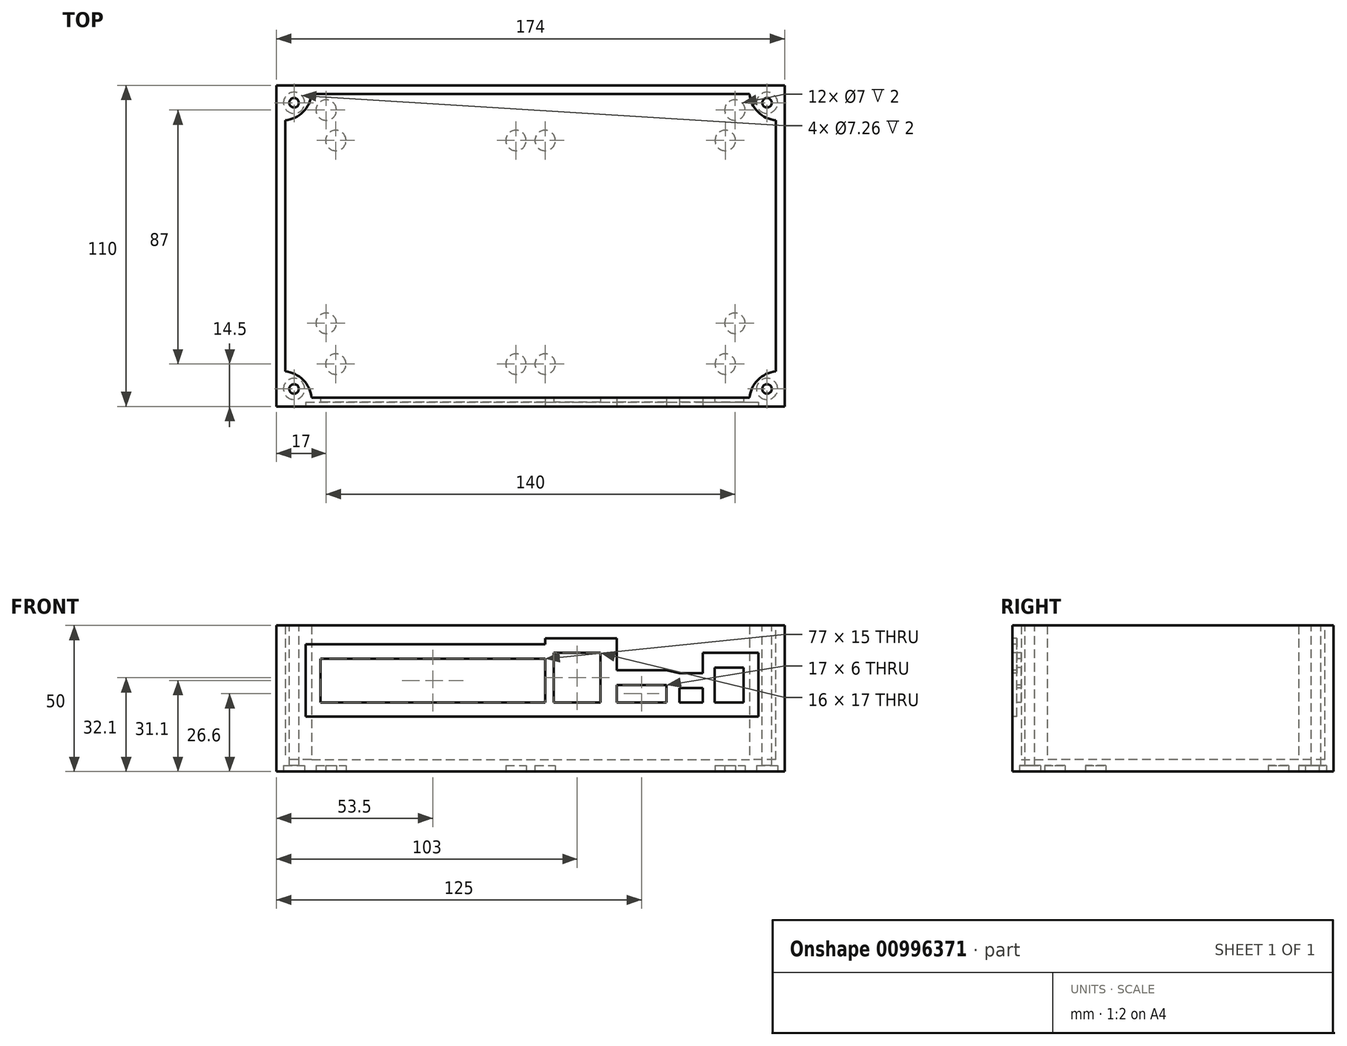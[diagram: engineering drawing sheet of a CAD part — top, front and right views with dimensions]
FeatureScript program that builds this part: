
annotation { "Feature Type Name" : "Feature", "Feature Type Description" : "" }
export const myFeature = defineFeature(function(context is Context, id is Id, definition is map)
    precondition{}
    {
        {
            var Q0;
            Q0=qCreatedBy(makeId("Top.planeOp"),FACE);
            var sketch = newSketch(context, id + "F0", { "sketchPlane" : qUnion([Q0])});
            skLineSegment(sketch, "E0.bottom", {"start": v(-87, -55) * mm, "end": v(87, -55) * mm});
            skLineSegment(sketch, "E0.top", {"start": v(-87, 55) * mm, "end": v(87, 55) * mm});
            skLineSegment(sketch, "E0.left", {"start": v(-87, -55) * mm, "end": v(-87, 55) * mm});
            skLineSegment(sketch, "E0.right", {"start": v(87, -55) * mm, "end": v(87, 55) * mm});
            skPoint(sketch, "E0.middle", {"position": v(0, 0) * mm});
            skSolve(sketch);
        }
        {
            var Q0;
            Q0=makeQuery(id+"F0.imprint","IMPRINT",FACE,{"disambiguationData":[TD([[makeQuery(id+"F0.imprint","IMPRINT",EDGE,{"derivedFrom":sQuery(id+"F0.wireOp",EDGE,"E0.bottom")}),1.0]])]});
            extrude(context, id + "F1", {"entities" : qUnion([Q0]), "depth" : -4 * mm, "offsetDistance" : 25 * mm});
        }
        {
            var Q0;
            Q0=makeQuery(id+"F1.opExtrude","CAP_FACE",FACE,{"disambiguationData":[OSD([sQuery(id+"F0.wireOp",EDGE,"E0.bottom"),sQuery(id+"F0.wireOp",EDGE,"E0.top"),sQuery(id+"F0.wireOp",EDGE,"E0.left"),sQuery(id+"F0.wireOp",EDGE,"E0.right")])],"isStart":true});
            var sketch = newSketch(context, id + "F2", { "sketchPlane" : qUnion([Q0])});
            skLineSegment(sketch, "E1.bottom", {"start": v(-84, 52) * mm, "end": v(84, 52) * mm});
            skLineSegment(sketch, "E1.top", {"start": v(-84, -52) * mm, "end": v(84, -52) * mm});
            skLineSegment(sketch, "E1.left", {"start": v(-84, 52) * mm, "end": v(-84, -52) * mm});
            skLineSegment(sketch, "E1.right", {"start": v(84, 52) * mm, "end": v(84, -52) * mm});
            skPoint(sketch, "E1.middle", {"position": v(0, 0) * mm});
            skLineSegment(sketch, "E2.0", {"start": v(-87, 55) * mm, "end": v(87, 55) * mm});
            skLineSegment(sketch, "E2.1", {"start": v(-87, 55) * mm, "end": v(-87, -55) * mm});
            skLineSegment(sketch, "E2.2", {"start": v(-87, -55) * mm, "end": v(87, -55) * mm});
            skLineSegment(sketch, "E2.3", {"start": v(87, 55) * mm, "end": v(87, -55) * mm});
            skSolve(sketch);
        }
        {
            var Q0;
            Q0=makeQuery(id+"F2.imprint","IMPRINT",FACE,{"disambiguationData":[TD([[makeQuery(id+"F2.imprint","IMPRINT",EDGE,{"derivedFrom":sQuery(id+"F2.wireOp",EDGE,"E1.bottom")}),1.0]])]});
            extrude(context, id + "F3", {"entities" : qUnion([Q0]), "operationType" : NewBodyOperationType.ADD, "depth" : 46 * mm, "offsetDistance" : 25 * mm});
        }
        {
            var Q0;
            Q0=makeQuery(id+"F1.opExtrude","CAP_FACE",FACE,{"disambiguationData":[OSD([sQuery(id+"F0.wireOp",EDGE,"E0.bottom"),sQuery(id+"F0.wireOp",EDGE,"E0.top"),sQuery(id+"F0.wireOp",EDGE,"E0.left"),sQuery(id+"F0.wireOp",EDGE,"E0.right")])],"isStart":false});
            var sketch = newSketch(context, id + "F4", { "sketchPlane" : qUnion([Q0])});
            skLineSegment(sketch, "E3.bottom", {"start": v(-74, 50.5) * mm, "end": v(74, 50.5) * mm});
            skLineSegment(sketch, "E3.top", {"start": v(-74, -50.5) * mm, "end": v(74, -50.5) * mm});
            skLineSegment(sketch, "E3.left", {"start": v(-74, 50.5) * mm, "end": v(-74, -50.5) * mm});
            skLineSegment(sketch, "E3.right", {"start": v(74, 50.5) * mm, "end": v(74, -50.5) * mm});
            skPoint(sketch, "E3.middle", {"position": v(0, 0) * mm});
            skLineSegment(sketch, "E4.bottom", {"start": v(-65.7, 44.5) * mm, "end": v(-4, 44.5) * mm, "construction": true});
            skLineSegment(sketch, "E4.top", {"start": v(-65.7, -32.1) * mm, "end": v(-4, -32.1) * mm, "construction": true});
            skLineSegment(sketch, "E4.left", {"start": v(-65.7, 44.5) * mm, "end": v(-65.7, -32.1) * mm, "construction": true});
            skLineSegment(sketch, "E4.right", {"start": v(-4, 44.5) * mm, "end": v(-4, -32.1) * mm, "construction": true});
            skLineSegment(sketch, "E5.bottom", {"start": v(4, 44.5) * mm, "end": v(65.7, 44.5) * mm, "construction": true});
            skLineSegment(sketch, "E5.top", {"start": v(4, -32.1) * mm, "end": v(65.7, -32.1) * mm, "construction": true});
            skLineSegment(sketch, "E5.left", {"start": v(4, 44.5) * mm, "end": v(4, -32.1) * mm, "construction": true});
            skLineSegment(sketch, "E5.right", {"start": v(65.7, 44.5) * mm, "end": v(65.7, -32.1) * mm, "construction": true});
            skCircle(sketch, "E6", {"center": v(-65.7, 44.5) * mm, "radius": 1.63 * mm});
            skCircle(sketch, "E7", {"center": v(-4, 44.5) * mm, "radius": 1.63 * mm});
            skCircle(sketch, "E8", {"center": v(-65.7, -32.1) * mm, "radius": 1.63 * mm});
            skCircle(sketch, "E9", {"center": v(-4, -32.1) * mm, "radius": 1.63 * mm});
            skCircle(sketch, "E10", {"center": v(4, -32.1) * mm, "radius": 1.63 * mm});
            skCircle(sketch, "E11", {"center": v(65.7, -32.1) * mm, "radius": 1.63 * mm});
            skCircle(sketch, "E12", {"center": v(65.7, 44.5) * mm, "radius": 1.63 * mm});
            skCircle(sketch, "E13", {"center": v(4, 44.5) * mm, "radius": 1.5 * mm});
            skCircle(sketch, "E14.0", {"center": v(-65.7, 44.5) * mm, "radius": 3.63 * mm});
            skCircle(sketch, "E15.0", {"center": v(-4, 44.5) * mm, "radius": 3.63 * mm});
            skCircle(sketch, "E16.0", {"center": v(4, 44.5) * mm, "radius": 3.5 * mm});
            skCircle(sketch, "E17.0", {"center": v(65.7, 44.5) * mm, "radius": 3.63 * mm});
            skCircle(sketch, "E18.0", {"center": v(65.7, -32.1) * mm, "radius": 3.63 * mm});
            skCircle(sketch, "E19.0", {"center": v(4, -32.1) * mm, "radius": 3.63 * mm});
            skCircle(sketch, "E20.0", {"center": v(-4, -32.1) * mm, "radius": 3.63 * mm});
            skCircle(sketch, "E21.0", {"center": v(-65.7, -32.1) * mm, "radius": 3.63 * mm});
            skCircle(sketch, "E22", {"center": v(-70, -46.5) * mm, "radius": 1.63 * mm});
            skCircle(sketch, "E23.0", {"center": v(-70, -46.5) * mm, "radius": 3.63 * mm});
            skCircle(sketch, "E24", {"center": v(-70, 26.5) * mm, "radius": 1.63 * mm});
            skCircle(sketch, "E25.0", {"center": v(-70, 26.5) * mm, "radius": 3.63 * mm});
            skCircle(sketch, "E26", {"center": v(70, -46.5) * mm, "radius": 1.63 * mm});
            skCircle(sketch, "E27.0", {"center": v(70, -46.5) * mm, "radius": 3.63 * mm});
            skCircle(sketch, "E28", {"center": v(70, 26.5) * mm, "radius": 1.63 * mm});
            skCircle(sketch, "E29.0", {"center": v(70, 26.5) * mm, "radius": 3.63 * mm});
            skSolve(sketch);
        }
        {
            var Q0;
            Q0=makeQuery(id+"F1.opExtrude","CAP_FACE",FACE,{"disambiguationData":[OSD([sQuery(id+"F0.wireOp",EDGE,"E0.bottom"),sQuery(id+"F0.wireOp",EDGE,"E0.top"),sQuery(id+"F0.wireOp",EDGE,"E0.left"),sQuery(id+"F0.wireOp",EDGE,"E0.right")])],"isStart":false});
            var sketch = newSketch(context, id + "F5", { "sketchPlane" : qUnion([Q0])});
            skCircle(sketch, "E30.0", {"center": v(-66.7, 40.5) * mm, "radius": 3.5 * mm});
            skCircle(sketch, "E31.0", {"center": v(-70, 26.5) * mm, "radius": 3.5 * mm});
            skCircle(sketch, "E32.0", {"center": v(-5, 40.5) * mm, "radius": 3.5 * mm});
            skCircle(sketch, "E33.0", {"center": v(5, 40.5) * mm, "radius": 3.5 * mm});
            skCircle(sketch, "E34.0", {"center": v(66.7, 40.5) * mm, "radius": 3.5 * mm});
            skCircle(sketch, "E35.0", {"center": v(70, 26.5) * mm, "radius": 3.5 * mm});
            skCircle(sketch, "E36.0", {"center": v(66.7, -36.1) * mm, "radius": 3.5 * mm});
            skCircle(sketch, "E37.0", {"center": v(70, -46.5) * mm, "radius": 3.5 * mm});
            skCircle(sketch, "E38.0", {"center": v(5, -36.1) * mm, "radius": 3.5 * mm});
            skCircle(sketch, "E39.0", {"center": v(-5, -36.1) * mm, "radius": 3.5 * mm});
            skCircle(sketch, "E40.0", {"center": v(-66.7, -36.1) * mm, "radius": 3.5 * mm});
            skCircle(sketch, "E41.0", {"center": v(-70, -46.5) * mm, "radius": 3.5 * mm});
            skLineSegment(sketch, "E42.0", {"start": v(-92, -60) * mm, "end": v(92, -60) * mm});
            skLineSegment(sketch, "E42.1", {"start": v(-92, 60) * mm, "end": v(-92, -60) * mm});
            skLineSegment(sketch, "E42.2", {"start": v(92, 60) * mm, "end": v(-92, 60) * mm});
            skLineSegment(sketch, "E42.3", {"start": v(92, -60) * mm, "end": v(92, 60) * mm});
            skSolve(sketch);
        }
        {
            var Q0;
            Q0=makeQuery(id+"F5.imprint","IMPRINT",FACE,{"disambiguationData":[TD([[makeQuery(id+"F5.imprint","IMPRINT",EDGE,{"derivedFrom":sQuery(id+"F5.wireOp",EDGE,"E30.0")}),1.0]])]});
            var Q1;
            Q1=makeQuery(id+"F5.imprint","IMPRINT",FACE,{"disambiguationData":[TD([[makeQuery(id+"F5.imprint","IMPRINT",EDGE,{"derivedFrom":sQuery(id+"F5.wireOp",EDGE,"E31.0")}),1.0]])]});
            var Q2;
            Q2=makeQuery(id+"F5.imprint","IMPRINT",FACE,{"disambiguationData":[TD([[makeQuery(id+"F5.imprint","IMPRINT",EDGE,{"derivedFrom":sQuery(id+"F5.wireOp",EDGE,"E40.0")}),1.0]])]});
            var Q3;
            Q3=makeQuery(id+"F5.imprint","IMPRINT",FACE,{"disambiguationData":[TD([[makeQuery(id+"F5.imprint","IMPRINT",EDGE,{"derivedFrom":sQuery(id+"F5.wireOp",EDGE,"E41.0")}),1.0]])]});
            var Q4;
            Q4=makeQuery(id+"F5.imprint","IMPRINT",FACE,{"disambiguationData":[TD([[makeQuery(id+"F5.imprint","IMPRINT",EDGE,{"derivedFrom":sQuery(id+"F5.wireOp",EDGE,"E39.0")}),1.0]])]});
            var Q5;
            Q5=makeQuery(id+"F5.imprint","IMPRINT",FACE,{"disambiguationData":[TD([[makeQuery(id+"F5.imprint","IMPRINT",EDGE,{"derivedFrom":sQuery(id+"F5.wireOp",EDGE,"E38.0")}),1.0]])]});
            var Q6;
            Q6=makeQuery(id+"F5.imprint","IMPRINT",FACE,{"disambiguationData":[TD([[makeQuery(id+"F5.imprint","IMPRINT",EDGE,{"derivedFrom":sQuery(id+"F5.wireOp",EDGE,"E32.0")}),1.0]])]});
            var Q7;
            Q7=makeQuery(id+"F5.imprint","IMPRINT",FACE,{"disambiguationData":[TD([[makeQuery(id+"F5.imprint","IMPRINT",EDGE,{"derivedFrom":sQuery(id+"F5.wireOp",EDGE,"E33.0")}),1.0]])]});
            var Q8;
            Q8=makeQuery(id+"F5.imprint","IMPRINT",FACE,{"disambiguationData":[TD([[makeQuery(id+"F5.imprint","IMPRINT",EDGE,{"derivedFrom":sQuery(id+"F5.wireOp",EDGE,"E34.0")}),1.0]])]});
            var Q9;
            Q9=makeQuery(id+"F5.imprint","IMPRINT",FACE,{"disambiguationData":[TD([[makeQuery(id+"F5.imprint","IMPRINT",EDGE,{"derivedFrom":sQuery(id+"F5.wireOp",EDGE,"E35.0")}),1.0]])]});
            var Q10;
            Q10=makeQuery(id+"F5.imprint","IMPRINT",FACE,{"disambiguationData":[TD([[makeQuery(id+"F5.imprint","IMPRINT",EDGE,{"derivedFrom":sQuery(id+"F5.wireOp",EDGE,"E36.0")}),1.0]])]});
            var Q11;
            Q11=makeQuery(id+"F5.imprint","IMPRINT",FACE,{"disambiguationData":[TD([[makeQuery(id+"F5.imprint","IMPRINT",EDGE,{"derivedFrom":sQuery(id+"F5.wireOp",EDGE,"E37.0")}),1.0]])]});
            extrude(context, id + "F6", {"entities" : qUnion([Q0, Q1, Q2, Q3, Q4, Q5, Q6, Q7, Q8, Q9, Q10, Q11]), "operationType" : NewBodyOperationType.REMOVE, "depth" : -2 * mm, "offsetDistance" : 25 * mm});
        }
        {
            var Q0;
            Q0=makeQuery(id+"F3.boolean.opBoolean","MERGE",FACE,{"derivedFrom":[makeQuery(id+"F1.opExtrude","SWEPT_FACE",FACE,{"disambiguationData":[OSD([sQuery(id+"F0.wireOp",EDGE,"E0.bottom")])]}),makeQuery(id+"F3.opExtrude","SWEPT_FACE",FACE,{"disambiguationData":[OSD([sQuery(id+"F2.wireOp",EDGE,"E2.2")])]})]});
            var sketch = newSketch(context, id + "F7", { "sketchPlane" : qUnion([Q0])});
            skLineSegment(sketch, "E43", {"start": v(-100.46, 19.6) * mm, "end": v(103.84, 19.6) * mm, "construction": true});
            skLineSegment(sketch, "E44", {"start": v(0, -31) * mm, "end": v(0, 52.42) * mm, "construction": true});
            skLineSegment(sketch, "E45.bottom", {"start": v(-74, 59.6) * mm, "end": v(74, 59.6) * mm, "construction": true});
            skLineSegment(sketch, "E45.top", {"start": v(-74, -20.4) * mm, "end": v(74, -20.4) * mm, "construction": true});
            skLineSegment(sketch, "E45.left", {"start": v(-74, 59.6) * mm, "end": v(-74, -20.4) * mm, "construction": true});
            skLineSegment(sketch, "E45.right", {"start": v(74, 59.6) * mm, "end": v(74, -20.4) * mm, "construction": true});
            skPoint(sketch, "E45.middle", {"position": v(0, 19.6) * mm});
            skLineSegment(sketch, "E46", {"start": v(-33.5, 53.59) * mm, "end": v(-33.5, -6.96) * mm, "construction": true});
            skLineSegment(sketch, "E47", {"start": v(16, 52.07) * mm, "end": v(16, -12.35) * mm, "construction": true});
            skLineSegment(sketch, "E48", {"start": v(38, 50.3) * mm, "end": v(38, -12.83) * mm, "construction": true});
            skLineSegment(sketch, "E49", {"start": v(55, 49.17) * mm, "end": v(55, -12.18) * mm, "construction": true});
            skLineSegment(sketch, "E50", {"start": v(68, 54.65) * mm, "end": v(68, -10.1) * mm, "construction": true});
            skPoint(sketch, "E51.middle", {"position": v(16, 19.6) * mm});
            skPoint(sketch, "E52.middle", {"position": v(38, 19.6) * mm});
            skPoint(sketch, "E53.middle", {"position": v(55, 19.6) * mm});
            skPoint(sketch, "E54.middle", {"position": v(68, 19.6) * mm});
            skPoint(sketch, "E55.middle", {"position": v(-33.5, 19.6) * mm});
            skLineSegment(sketch, "E56.bottom", {"start": v(-33.5, 19.6) * mm, "end": v(-72, 19.6) * mm});
            skLineSegment(sketch, "E56.top", {"start": v(-33.5, 34.6) * mm, "end": v(-72, 34.6) * mm});
            skLineSegment(sketch, "E56.left", {"start": v(-33.5, 19.6) * mm, "end": v(-33.5, 34.6) * mm});
            skLineSegment(sketch, "E56.right", {"start": v(-72, 19.6) * mm, "end": v(-72, 34.6) * mm});
            skLineSegment(sketch, "E57.bottom", {"start": v(-33.5, 19.6) * mm, "end": v(5, 19.6) * mm});
            skLineSegment(sketch, "E57.top", {"start": v(-33.5, 34.6) * mm, "end": v(5, 34.6) * mm});
            skLineSegment(sketch, "E57.right", {"start": v(5, 19.6) * mm, "end": v(5, 34.6) * mm});
            skLineSegment(sketch, "E58.bottom", {"start": v(16, 19.6) * mm, "end": v(8, 19.6) * mm});
            skLineSegment(sketch, "E58.top", {"start": v(16, 36.6) * mm, "end": v(8, 36.6) * mm});
            skLineSegment(sketch, "E58.left", {"start": v(16, 19.6) * mm, "end": v(16, 36.6) * mm});
            skLineSegment(sketch, "E58.right", {"start": v(8, 19.6) * mm, "end": v(8, 36.6) * mm});
            skLineSegment(sketch, "E59.bottom", {"start": v(16, 19.6) * mm, "end": v(24, 19.6) * mm});
            skLineSegment(sketch, "E59.top", {"start": v(16, 36.6) * mm, "end": v(24, 36.6) * mm});
            skLineSegment(sketch, "E59.right", {"start": v(24, 19.6) * mm, "end": v(24, 36.6) * mm});
            skLineSegment(sketch, "E60.bottom", {"start": v(38, 19.6) * mm, "end": v(29.5, 19.6) * mm});
            skLineSegment(sketch, "E60.top", {"start": v(38, 25.6) * mm, "end": v(29.5, 25.6) * mm});
            skLineSegment(sketch, "E60.left", {"start": v(38, 19.6) * mm, "end": v(38, 25.6) * mm});
            skLineSegment(sketch, "E60.right", {"start": v(29.5, 19.6) * mm, "end": v(29.5, 25.6) * mm});
            skLineSegment(sketch, "E61.bottom", {"start": v(38, 19.6) * mm, "end": v(46.5, 19.6) * mm});
            skLineSegment(sketch, "E61.top", {"start": v(38, 25.6) * mm, "end": v(46.5, 25.6) * mm});
            skLineSegment(sketch, "E61.right", {"start": v(46.5, 19.6) * mm, "end": v(46.5, 25.6) * mm});
            skLineSegment(sketch, "E62.bottom", {"start": v(55, 19.6) * mm, "end": v(51, 19.6) * mm});
            skLineSegment(sketch, "E62.top", {"start": v(55, 24.6) * mm, "end": v(51, 24.6) * mm});
            skLineSegment(sketch, "E62.left", {"start": v(55, 19.6) * mm, "end": v(55, 24.6) * mm});
            skLineSegment(sketch, "E62.right", {"start": v(51, 19.6) * mm, "end": v(51, 24.6) * mm});
            skLineSegment(sketch, "E63.bottom", {"start": v(55, 19.6) * mm, "end": v(59, 19.6) * mm});
            skLineSegment(sketch, "E63.top", {"start": v(55, 24.6) * mm, "end": v(59, 24.6) * mm});
            skLineSegment(sketch, "E63.right", {"start": v(59, 19.6) * mm, "end": v(59, 24.6) * mm});
            skLineSegment(sketch, "E64.bottom", {"start": v(68, 19.6) * mm, "end": v(63, 19.6) * mm});
            skLineSegment(sketch, "E64.top", {"start": v(68, 31.6) * mm, "end": v(63, 31.6) * mm});
            skLineSegment(sketch, "E64.left", {"start": v(68, 19.6) * mm, "end": v(68, 31.6) * mm});
            skLineSegment(sketch, "E64.right", {"start": v(63, 19.6) * mm, "end": v(63, 31.6) * mm});
            skLineSegment(sketch, "E65.bottom", {"start": v(68, 19.6) * mm, "end": v(73, 19.6) * mm});
            skLineSegment(sketch, "E65.top", {"start": v(68, 31.6) * mm, "end": v(73, 31.6) * mm});
            skLineSegment(sketch, "E65.right", {"start": v(73, 19.6) * mm, "end": v(73, 31.6) * mm});
            skLineSegment(sketch, "E66.0", {"start": v(-77, 19.8) * mm, "end": v(-77, 34.6) * mm});
            skLineSegment(sketch, "E67.0", {"start": v(-33.5, 39.6) * mm, "end": v(-72, 39.6) * mm});
            skLineSegment(sketch, "E68.0", {"start": v(-33.5, 39.6) * mm, "end": v(5, 39.6) * mm});
            skLineSegment(sketch, "E69.0", {"start": v(16, 41.6) * mm, "end": v(8, 41.6) * mm});
            skLineSegment(sketch, "E70.0", {"start": v(16, 41.6) * mm, "end": v(24, 41.6) * mm});
            skLineSegment(sketch, "E71.0", {"start": v(38, 30.6) * mm, "end": v(29.5, 30.6) * mm});
            skLineSegment(sketch, "E72.0", {"start": v(38, 30.6) * mm, "end": v(46.5, 30.6) * mm});
            skLineSegment(sketch, "E73.0", {"start": v(55, 29.6) * mm, "end": v(51, 29.6) * mm});
            skLineSegment(sketch, "E74.0", {"start": v(55, 29.6) * mm, "end": v(59, 29.6) * mm});
            skLineSegment(sketch, "E75.0", {"start": v(68, 36.6) * mm, "end": v(63, 36.6) * mm});
            skLineSegment(sketch, "E76.0", {"start": v(68, 36.6) * mm, "end": v(73, 36.6) * mm});
            skLineSegment(sketch, "E77.0", {"start": v(78, 19.6) * mm, "end": v(78, 31.6) * mm});
            skLineSegment(sketch, "E78", {"start": v(-77, 34.6) * mm, "end": v(-77, 39.6) * mm});
            skLineSegment(sketch, "E79", {"start": v(-77, 39.6) * mm, "end": v(-72, 39.6) * mm});
            skLineSegment(sketch, "E80", {"start": v(5, 39.6) * mm, "end": v(5, 41.6) * mm});
            skLineSegment(sketch, "E81", {"start": v(5, 41.6) * mm, "end": v(8, 41.6) * mm});
            skLineSegment(sketch, "E82", {"start": v(24, 41.6) * mm, "end": v(29.5, 41.6) * mm});
            skLineSegment(sketch, "E83", {"start": v(29.5, 41.6) * mm, "end": v(29.5, 30.6) * mm});
            skLineSegment(sketch, "E84", {"start": v(46.5, 30.6) * mm, "end": v(51, 29.6) * mm});
            skLineSegment(sketch, "E85", {"start": v(59, 29.6) * mm, "end": v(59, 36.6) * mm});
            skLineSegment(sketch, "E86", {"start": v(59, 36.6) * mm, "end": v(63, 36.6) * mm});
            skLineSegment(sketch, "E87", {"start": v(73, 36.6) * mm, "end": v(78, 36.6) * mm});
            skLineSegment(sketch, "E88", {"start": v(78, 36.6) * mm, "end": v(78, 31.6) * mm});
            skLineSegment(sketch, "E89", {"start": v(-77, 19.8) * mm, "end": v(-77, 14.8) * mm});
            skLineSegment(sketch, "E90", {"start": v(-77, 14.8) * mm, "end": v(78, 14.8) * mm});
            skLineSegment(sketch, "E91", {"start": v(78, 14.8) * mm, "end": v(78, 19.6) * mm});
            skSolve(sketch);
        }
        {
            var Q0;
            Q0=makeQuery(id+"F7.imprint","IMPRINT",FACE,{"disambiguationData":[TD([[makeQuery(id+"F7.imprint","IMPRINT",EDGE,{"derivedFrom":sQuery(id+"F7.wireOp",EDGE,"E56.bottom")}),-1.0]])]});
            var Q1;
            Q1=makeQuery(id+"F7.imprint","IMPRINT",FACE,{"disambiguationData":[TD([[makeQuery(id+"F7.imprint","IMPRINT",EDGE,{"derivedFrom":sQuery(id+"F7.wireOp",EDGE,"E57.bottom")}),1.0]])]});
            var Q2;
            Q2=makeQuery(id+"F7.imprint","IMPRINT",FACE,{"disambiguationData":[TD([[makeQuery(id+"F7.imprint","IMPRINT",EDGE,{"derivedFrom":sQuery(id+"F7.wireOp",EDGE,"E58.bottom")}),-1.0]])]});
            var Q3;
            Q3=makeQuery(id+"F7.imprint","IMPRINT",FACE,{"disambiguationData":[TD([[makeQuery(id+"F7.imprint","IMPRINT",EDGE,{"derivedFrom":sQuery(id+"F7.wireOp",EDGE,"E59.bottom")}),1.0]])]});
            var Q4;
            Q4=makeQuery(id+"F7.imprint","IMPRINT",FACE,{"disambiguationData":[TD([[makeQuery(id+"F7.imprint","IMPRINT",EDGE,{"derivedFrom":sQuery(id+"F7.wireOp",EDGE,"E60.bottom")}),-1.0]])]});
            var Q5;
            Q5=makeQuery(id+"F7.imprint","IMPRINT",FACE,{"disambiguationData":[TD([[makeQuery(id+"F7.imprint","IMPRINT",EDGE,{"derivedFrom":sQuery(id+"F7.wireOp",EDGE,"E61.bottom")}),1.0]])]});
            var Q6;
            Q6=makeQuery(id+"F7.imprint","IMPRINT",FACE,{"disambiguationData":[TD([[makeQuery(id+"F7.imprint","IMPRINT",EDGE,{"derivedFrom":sQuery(id+"F7.wireOp",EDGE,"E62.bottom")}),-1.0]])]});
            var Q7;
            Q7=makeQuery(id+"F7.imprint","IMPRINT",FACE,{"disambiguationData":[TD([[makeQuery(id+"F7.imprint","IMPRINT",EDGE,{"derivedFrom":sQuery(id+"F7.wireOp",EDGE,"E63.bottom")}),1.0]])]});
            var Q8;
            Q8=makeQuery(id+"F7.imprint","IMPRINT",FACE,{"disambiguationData":[TD([[makeQuery(id+"F7.imprint","IMPRINT",EDGE,{"derivedFrom":sQuery(id+"F7.wireOp",EDGE,"E64.bottom")}),-1.0]])]});
            var Q9;
            Q9=makeQuery(id+"F7.imprint","IMPRINT",FACE,{"disambiguationData":[TD([[makeQuery(id+"F7.imprint","IMPRINT",EDGE,{"derivedFrom":sQuery(id+"F7.wireOp",EDGE,"E65.bottom")}),1.0]])]});
            extrude(context, id + "F8", {"entities" : qUnion([Q0, Q1, Q2, Q3, Q4, Q5, Q6, Q7, Q8, Q9]), "operationType" : NewBodyOperationType.REMOVE, "oppositeDirection" : true, "depth" : 3 * mm, "offsetDistance" : 25 * mm});
        }
        {
            var Q0;
            Q0=makeQuery(id+"F3.opExtrude","CAP_FACE",FACE,{"disambiguationData":[OSD([sQuery(id+"F2.wireOp",EDGE,"E1.bottom"),sQuery(id+"F2.wireOp",EDGE,"E1.top"),sQuery(id+"F2.wireOp",EDGE,"E1.left"),sQuery(id+"F2.wireOp",EDGE,"E1.right"),sQuery(id+"F2.wireOp",EDGE,"E2.0"),sQuery(id+"F2.wireOp",EDGE,"E2.1"),sQuery(id+"F2.wireOp",EDGE,"E2.2"),sQuery(id+"F2.wireOp",EDGE,"E2.3")])],"isStart":false});
            var sketch = newSketch(context, id + "F9", { "sketchPlane" : qUnion([Q0])});
            skLineSegment(sketch, "E92.bottom", {"start": v(-87, 55) * mm, "end": v(-75, 55) * mm});
            skLineSegment(sketch, "E92.top", {"start": v(-87, 43) * mm, "end": v(-75, 43) * mm});
            skLineSegment(sketch, "E92.left", {"start": v(-87, 55) * mm, "end": v(-87, 43) * mm});
            skLineSegment(sketch, "E92.right", {"start": v(-75, 55) * mm, "end": v(-75, 43) * mm});
            skLineSegment(sketch, "E93.bottom", {"start": v(87, 55) * mm, "end": v(75, 55) * mm});
            skLineSegment(sketch, "E93.top", {"start": v(87, 43) * mm, "end": v(75, 43) * mm});
            skLineSegment(sketch, "E93.left", {"start": v(87, 55) * mm, "end": v(87, 43) * mm});
            skLineSegment(sketch, "E93.right", {"start": v(75, 55) * mm, "end": v(75, 43) * mm});
            skLineSegment(sketch, "E94.bottom", {"start": v(87, -55) * mm, "end": v(75, -55) * mm});
            skLineSegment(sketch, "E94.top", {"start": v(87, -43) * mm, "end": v(75, -43) * mm});
            skLineSegment(sketch, "E94.left", {"start": v(87, -55) * mm, "end": v(87, -43) * mm});
            skLineSegment(sketch, "E94.right", {"start": v(75, -55) * mm, "end": v(75, -43) * mm});
            skLineSegment(sketch, "E95.bottom", {"start": v(-87, -55) * mm, "end": v(-75, -55) * mm});
            skLineSegment(sketch, "E95.top", {"start": v(-87, -43) * mm, "end": v(-75, -43) * mm});
            skLineSegment(sketch, "E95.left", {"start": v(-87, -55) * mm, "end": v(-87, -43) * mm});
            skLineSegment(sketch, "E95.right", {"start": v(-75, -55) * mm, "end": v(-75, -43) * mm});
            skCircle(sketch, "E96", {"center": v(-81, 49) * mm, "radius": 1.63 * mm});
            skPoint(sketch, "E96.centerSnap0", {"position": v(-81, 55) * mm});
            skPoint(sketch, "E96.centerSnap1", {"position": v(-87, 49) * mm});
            skCircle(sketch, "E97", {"center": v(81, 49) * mm, "radius": 1.63 * mm});
            skPoint(sketch, "E97.centerSnap0", {"position": v(75, 49) * mm});
            skPoint(sketch, "E97.centerSnap1", {"position": v(81, 43) * mm});
            skCircle(sketch, "E98", {"center": v(-81, -49) * mm, "radius": 1.63 * mm});
            skPoint(sketch, "E98.centerSnap0", {"position": v(-87, -49) * mm});
            skPoint(sketch, "E98.centerSnap1", {"position": v(-81, -43) * mm});
            skCircle(sketch, "E99", {"center": v(81, -49) * mm, "radius": 1.63 * mm});
            skPoint(sketch, "E99.centerSnap0", {"position": v(81, -55) * mm});
            skPoint(sketch, "E99.centerSnap1", {"position": v(87, -49) * mm});
            skSolve(sketch);
        }
        {
            var Q0;
            Q0=makeQuery(id+"F9.imprint","IMPRINT",FACE,{"disambiguationData":[TD([[makeQuery(id+"F9.imprint","IMPRINT",EDGE,{"derivedFrom":sQuery(id+"F9.wireOp",EDGE,"E96")}),-1.0]])]});
            var Q1;
            {var subQ1=sQuery(id+"F9.wireOp",EDGE,"E92.bottom");Q1=makeQuery(id+"F9.imprint","IMPRINT",FACE,{"disambiguationData":[TD([[makeQuery(id+"F9.imprint","IMPRINT",EDGE,{"derivedFrom":subQ1}),-1.0]])]});}
            var Q2;
            {var subQ1=sQuery(id+"F9.wireOp",EDGE,"E93.bottom");Q2=makeQuery(id+"F9.imprint","IMPRINT",FACE,{"disambiguationData":[TD([[makeQuery(id+"F9.imprint","IMPRINT",EDGE,{"derivedFrom":subQ1}),-1.0]])]});}
            var Q3;
            Q3=makeQuery(id+"F9.imprint","IMPRINT",FACE,{"disambiguationData":[TD([[makeQuery(id+"F9.imprint","IMPRINT",EDGE,{"derivedFrom":sQuery(id+"F9.wireOp",EDGE,"E97")}),-1.0]])]});
            var Q4;
            {var subQ1=sQuery(id+"F9.wireOp",EDGE,"E94.bottom");Q4=makeQuery(id+"F9.imprint","IMPRINT",FACE,{"disambiguationData":[TD([[makeQuery(id+"F9.imprint","IMPRINT",EDGE,{"derivedFrom":subQ1}),1.0]])]});}
            var Q5;
            Q5=makeQuery(id+"F9.imprint","IMPRINT",FACE,{"disambiguationData":[TD([[makeQuery(id+"F9.imprint","IMPRINT",EDGE,{"derivedFrom":sQuery(id+"F9.wireOp",EDGE,"E99")}),-1.0]])]});
            var Q6;
            Q6=makeQuery(id+"F9.imprint","IMPRINT",FACE,{"disambiguationData":[TD([[makeQuery(id+"F9.imprint","IMPRINT",EDGE,{"derivedFrom":sQuery(id+"F9.wireOp",EDGE,"E98")}),-1.0]])]});
            var Q7;
            {var subQ1=sQuery(id+"F9.wireOp",EDGE,"E95.bottom");Q7=makeQuery(id+"F9.imprint","IMPRINT",FACE,{"disambiguationData":[TD([[makeQuery(id+"F9.imprint","IMPRINT",EDGE,{"derivedFrom":subQ1}),1.0]])]});}
            extrude(context, id + "F10", {"entities" : qUnion([Q0, Q1, Q2, Q3, Q4, Q5, Q6, Q7]), "operationType" : NewBodyOperationType.ADD, "oppositeDirection" : true, "depth" : 46 * mm, "offsetDistance" : 25 * mm});
        }
        {
            var Q0;
            Q0=makeQuery(id+"F9.imprint","IMPRINT",FACE,{"disambiguationData":[TD([[makeQuery(id+"F9.imprint","IMPRINT",EDGE,{"derivedFrom":sQuery(id+"F9.wireOp",EDGE,"E96")}),1.0]])]});
            var Q1;
            Q1=makeQuery(id+"F9.imprint","IMPRINT",FACE,{"disambiguationData":[TD([[makeQuery(id+"F9.imprint","IMPRINT",EDGE,{"derivedFrom":sQuery(id+"F9.wireOp",EDGE,"E97")}),1.0]])]});
            var Q2;
            Q2=makeQuery(id+"F9.imprint","IMPRINT",FACE,{"disambiguationData":[TD([[makeQuery(id+"F9.imprint","IMPRINT",EDGE,{"derivedFrom":sQuery(id+"F9.wireOp",EDGE,"E99")}),1.0]])]});
            var Q3;
            Q3=makeQuery(id+"F9.imprint","IMPRINT",FACE,{"disambiguationData":[TD([[makeQuery(id+"F9.imprint","IMPRINT",EDGE,{"derivedFrom":sQuery(id+"F9.wireOp",EDGE,"E98")}),1.0]])]});
            extrude(context, id + "F11", {"entities" : qUnion([Q0, Q1, Q2, Q3]), "operationType" : NewBodyOperationType.REMOVE, "endBound" : BoundingType.THROUGH_ALL, "oppositeDirection" : true, "depth" : 25 * mm, "offsetDistance" : 25 * mm});
        }
        {
            var Q0;
            Q0=makeQuery(id+"F10.opExtrude","SWEPT_EDGE",EDGE,{"disambiguationData":[OSD([sQuery(id+"F9.wireOp",EDGE,"E92.top"),sQuery(id+"F9.wireOp",EDGE,"E92.right")])]});
            var Q1;
            Q1=makeQuery(id+"F10.opExtrude","SWEPT_EDGE",EDGE,{"disambiguationData":[OSD([sQuery(id+"F9.wireOp",EDGE,"E93.top"),sQuery(id+"F9.wireOp",EDGE,"E93.right")])]});
            var Q2;
            Q2=makeQuery(id+"F10.opExtrude","SWEPT_EDGE",EDGE,{"disambiguationData":[OSD([sQuery(id+"F9.wireOp",EDGE,"E95.top"),sQuery(id+"F9.wireOp",EDGE,"E95.right")])]});
            var Q3;
            Q3=makeQuery(id+"F10.opExtrude","SWEPT_EDGE",EDGE,{"disambiguationData":[OSD([sQuery(id+"F9.wireOp",EDGE,"E94.top"),sQuery(id+"F9.wireOp",EDGE,"E94.right")])]});
            fillet(context, id + "F12", {"entities" : qUnion([Q0, Q1, Q2, Q3]), "radius" : 10 * mm, "tangentPropagation" : true, "allowEdgeOverflow" : false});
        }
        {
            var Q0;
            Q0=makeQuery(id+"F1.opExtrude","CAP_FACE",FACE,{"disambiguationData":[OSD([sQuery(id+"F0.wireOp",EDGE,"E0.bottom"),sQuery(id+"F0.wireOp",EDGE,"E0.top"),sQuery(id+"F0.wireOp",EDGE,"E0.left"),sQuery(id+"F0.wireOp",EDGE,"E0.right")])],"isStart":false});
            var sketch = newSketch(context, id + "F13", { "sketchPlane" : qUnion([Q0])});
            skCircle(sketch, "E100.0", {"center": v(-81, 49) * mm, "radius": 3.63 * mm});
            skCircle(sketch, "E101.0", {"center": v(81, 49) * mm, "radius": 3.63 * mm});
            skCircle(sketch, "E102.0", {"center": v(81, -49) * mm, "radius": 3.63 * mm});
            skCircle(sketch, "E103.0", {"center": v(-81, -49) * mm, "radius": 3.63 * mm});
            skSolve(sketch);
        }
        {
            var Q0;
            Q0=makeQuery(id+"F13.imprint","IMPRINT",FACE,{"disambiguationData":[TD([[makeQuery(id+"F13.imprint","IMPRINT",EDGE,{"derivedFrom":sQuery(id+"F13.wireOp",EDGE,"E100.0")}),1.0]])]});
            var Q1;
            Q1=makeQuery(id+"F13.imprint","IMPRINT",FACE,{"disambiguationData":[TD([[makeQuery(id+"F13.imprint","IMPRINT",EDGE,{"derivedFrom":sQuery(id+"F13.wireOp",EDGE,"E101.0")}),1.0]])]});
            var Q2;
            Q2=makeQuery(id+"F13.imprint","IMPRINT",FACE,{"disambiguationData":[TD([[makeQuery(id+"F13.imprint","IMPRINT",EDGE,{"derivedFrom":sQuery(id+"F13.wireOp",EDGE,"E102.0")}),1.0]])]});
            var Q3;
            Q3=makeQuery(id+"F13.imprint","IMPRINT",FACE,{"disambiguationData":[TD([[makeQuery(id+"F13.imprint","IMPRINT",EDGE,{"derivedFrom":sQuery(id+"F13.wireOp",EDGE,"E103.0")}),1.0]])]});
            extrude(context, id + "F14", {"entities" : qUnion([Q0, Q1, Q2, Q3]), "operationType" : NewBodyOperationType.REMOVE, "oppositeDirection" : true, "depth" : 2 * mm, "offsetDistance" : 25 * mm});
        }
        {
            var Q0;
            Q0 = qSketchRegion(id + "F7", true);
            extrude(context, id + "F15", {"entities" : qUnion([Q0]), "operationType" : NewBodyOperationType.REMOVE, "oppositeDirection" : true, "depth" : 1.5 * mm, "offsetDistance" : 25 * mm});
        }
    });
